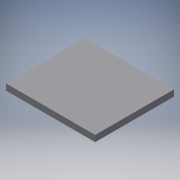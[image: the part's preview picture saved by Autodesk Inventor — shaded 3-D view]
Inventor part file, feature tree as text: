
AUTODESK INVENTOR PART (.ipt)
format: ipt  version: 2017 (Build 210142000, 142)  size: 88,576 bytes
history: native  units: in
note: dims shown in document units (in); Inventor stores cm internally (conversion verified against a paired STEP export)
features: extrude x1, sketch x1
ambient origin geometry x8: Origin, YZ Plane, XZ Plane, XY Plane, X Axis, Y Axis, Z Axis, Center Point
bodies: Solid1 (feature_tree)
feature tree (2):
  extrude  "Extrusion1"  Depth=9.5in
  sketch  "Sketch1"  dims[d0=10.75in d1=9.5in d2=0.75in d3=0.0in]
